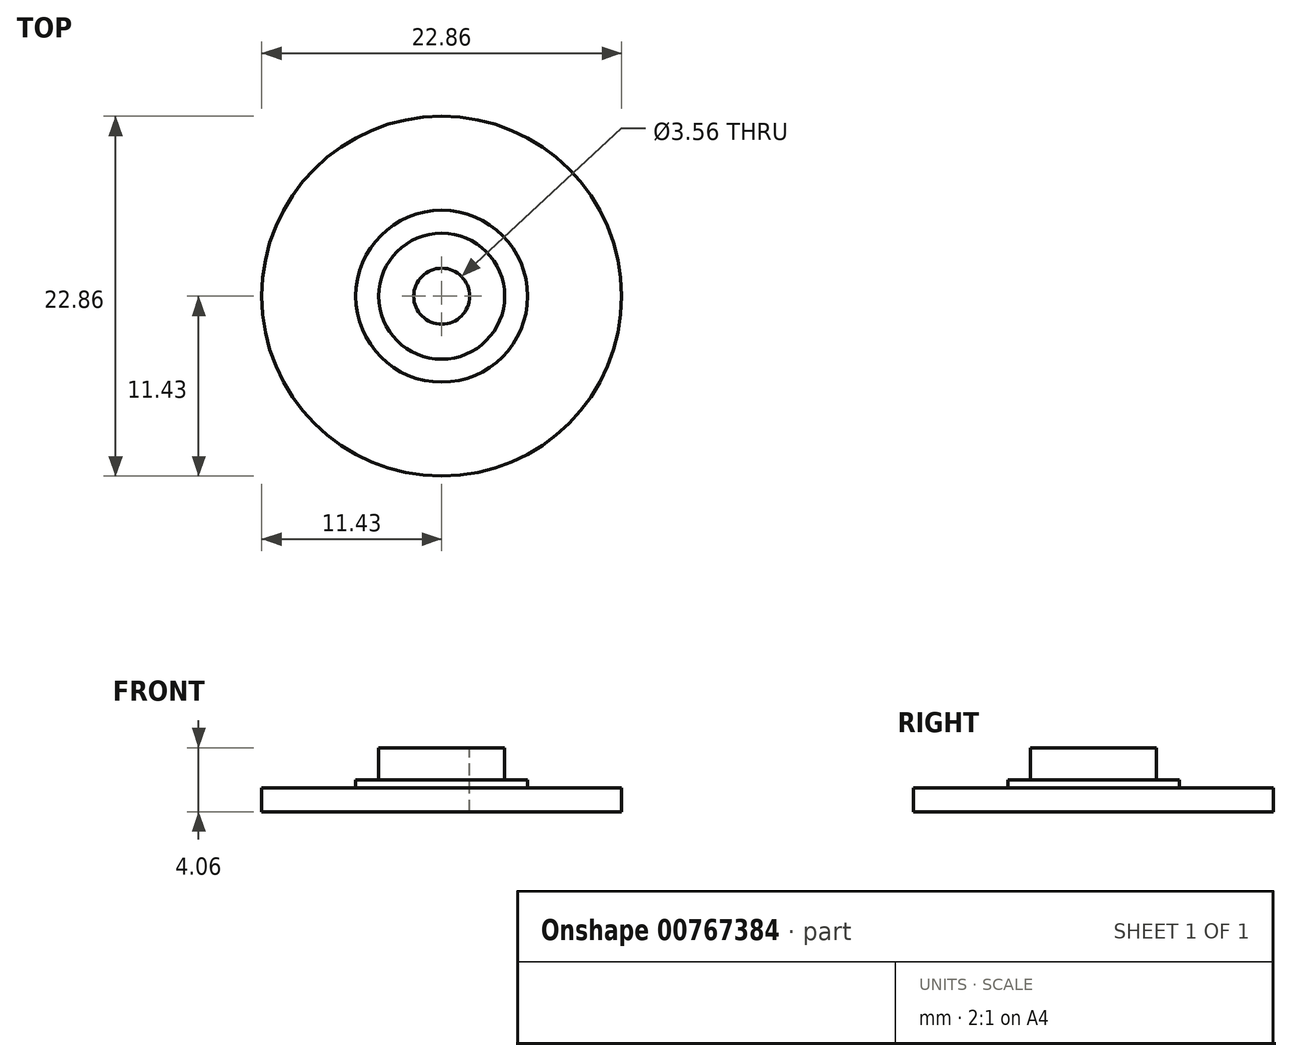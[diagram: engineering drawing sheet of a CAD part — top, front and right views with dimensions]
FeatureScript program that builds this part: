
annotation { "Feature Type Name" : "Feature", "Feature Type Description" : "" }
export const myFeature = defineFeature(function(context is Context, id is Id, definition is map)
    precondition{}
    {
        {
            var Q0;
            Q0=qCreatedBy(makeId("Top.planeOp"),FACE);
            var sketch = newSketch(context, id + "F0", { "sketchPlane" : qUnion([Q0])});
            skCircle(sketch, "E0", {"center": v(0, 0) * mm, "radius": 11.43 * mm});
            skSolve(sketch);
        }
        {
            var Q0;
            Q0=makeQuery(id+"F0.imprint","IMPRINT",FACE,{"disambiguationData":[TD([[makeQuery(id+"F0.imprint","IMPRINT",EDGE,{"derivedFrom":sQuery(id+"F0.wireOp",EDGE,"E0")}),1.0]])]});
            extrude(context, id + "F1", {"entities" : qUnion([Q0]), "depth" : 1.52 * mm, "offsetDistance" : 25.4 * mm});
        }
        {
            var Q0;
            Q0=makeQuery(id+"F1.opExtrude","CAP_FACE",FACE,{"disambiguationData":[OSD([sQuery(id+"F0.wireOp",EDGE,"E0")])],"isStart":false});
            var sketch = newSketch(context, id + "F2", { "sketchPlane" : qUnion([Q0])});
            skCircle(sketch, "E1", {"center": v(0, 0) * mm, "radius": 4 * mm});
            skSolve(sketch);
        }
        {
            var Q0;
            Q0=makeQuery(id+"F2.imprint","IMPRINT",FACE,{"disambiguationData":[TD([[makeQuery(id+"F2.imprint","IMPRINT",EDGE,{"derivedFrom":sQuery(id+"F2.wireOp",EDGE,"E1")}),1.0]])]});
            extrude(context, id + "F3", {"entities" : qUnion([Q0]), "operationType" : NewBodyOperationType.ADD, "depth" : 2.54 * mm, "offsetDistance" : 25.4 * mm});
        }
        {
            var Q0;
            Q0=makeQuery(id+"F3.opExtrude","CAP_FACE",FACE,{"disambiguationData":[OSD([sQuery(id+"F2.wireOp",EDGE,"E1")])],"isStart":false});
            var sketch = newSketch(context, id + "F4", { "sketchPlane" : qUnion([Q0])});
            skCircle(sketch, "E2", {"center": v(0, 0) * mm, "radius": 1.78 * mm});
            skSolve(sketch);
        }
        {
            var Q0;
            Q0=makeQuery(id+"F4.imprint","IMPRINT",FACE,{"disambiguationData":[TD([[makeQuery(id+"F4.imprint","IMPRINT",EDGE,{"derivedFrom":sQuery(id+"F4.wireOp",EDGE,"E2")}),1.0]])]});
            extrude(context, id + "F5", {"entities" : qUnion([Q0]), "operationType" : NewBodyOperationType.REMOVE, "oppositeDirection" : true, "depth" : 25.4 * mm, "offsetDistance" : 25.4 * mm});
        }
        {
            var Q0;
            Q0=makeQuery(id+"F1.opExtrude","CAP_FACE",FACE,{"disambiguationData":[OSD([sQuery(id+"F0.wireOp",EDGE,"E0")])],"isStart":false});
            var sketch = newSketch(context, id + "F6", { "sketchPlane" : qUnion([Q0])});
            skCircle(sketch, "E3", {"center": v(0, 0) * mm, "radius": 5.46 * mm});
            skSolve(sketch);
        }
        {
            var Q0;
            Q0=makeQuery(id+"F6.imprint","IMPRINT",FACE,{"disambiguationData":[TD([[makeQuery(id+"F6.imprint","IMPRINT",EDGE,{"derivedFrom":sQuery(id+"F6.wireOp",EDGE,"E3")}),1.0]])]});
            extrude(context, id + "F7", {"entities" : qUnion([Q0]), "operationType" : NewBodyOperationType.ADD, "depth" : 0.5 * mm, "offsetDistance" : 25.4 * mm});
        }
    });
